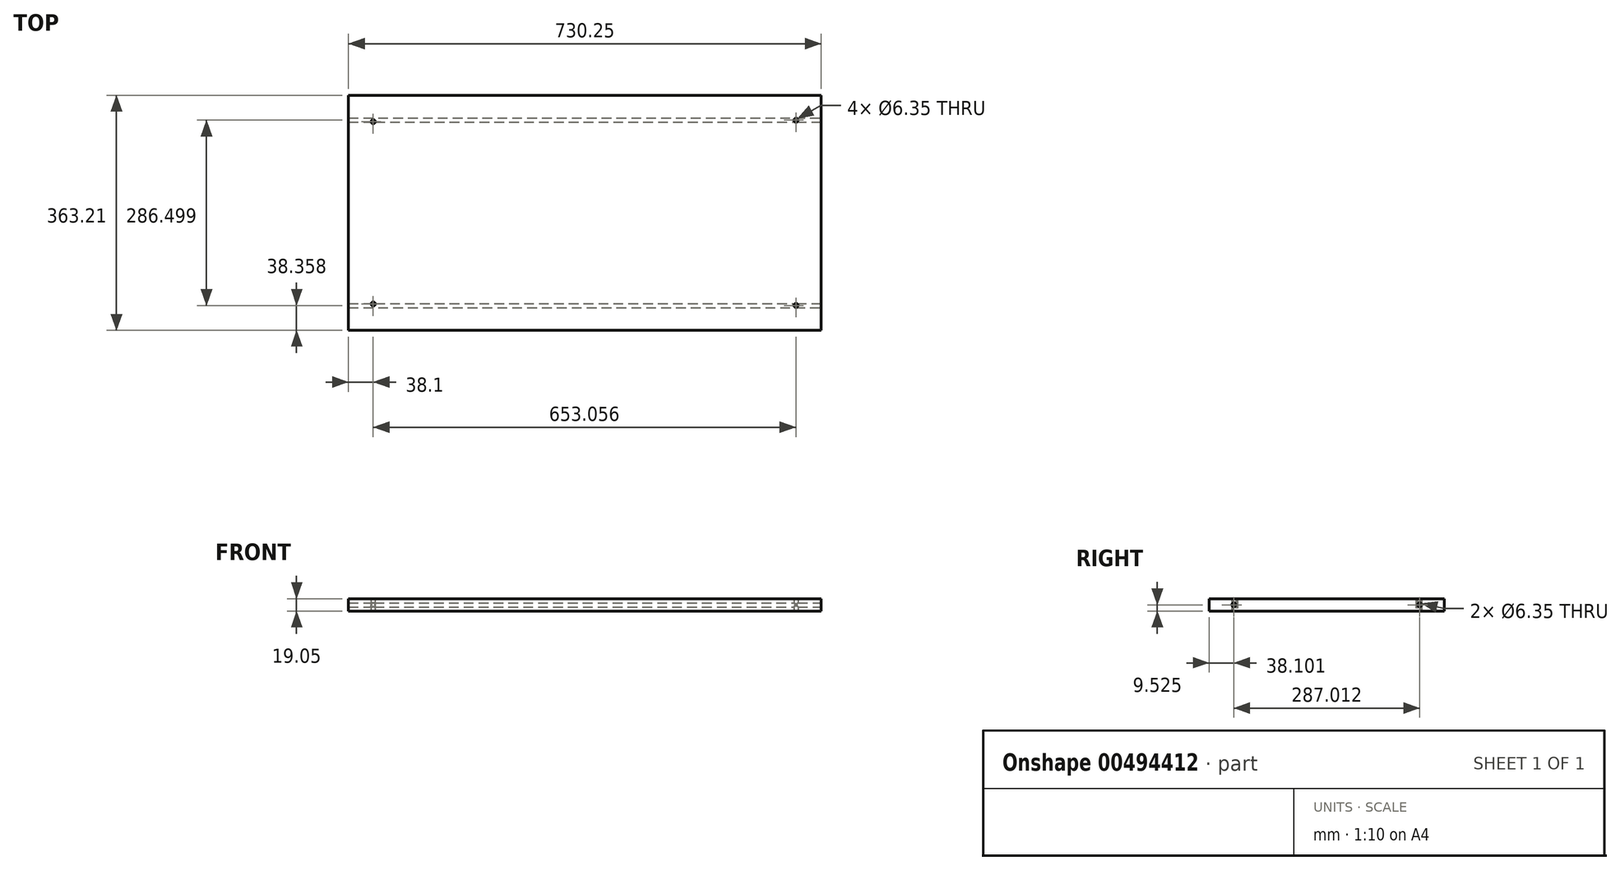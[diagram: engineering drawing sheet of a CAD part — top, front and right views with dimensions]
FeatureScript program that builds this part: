
annotation { "Feature Type Name" : "Feature", "Feature Type Description" : "" }
export const myFeature = defineFeature(function(context is Context, id is Id, definition is map)
    precondition{}
    {
        {
            var Q0;
            Q0=qCreatedBy(makeId("Top.planeOp"),FACE);
            var sketch = newSketch(context, id + "F0", { "sketchPlane" : qUnion([Q0])});
            skLineSegment(sketch, "E0.bottom", {"start": v(-364.5, 180.63) * mm, "end": v(365.76, 180.63) * mm});
            skLineSegment(sketch, "E0.top", {"start": v(-364.5, -182.58) * mm, "end": v(365.76, -182.58) * mm});
            skLineSegment(sketch, "E0.left", {"start": v(-364.5, 180.63) * mm, "end": v(-364.5, -182.58) * mm});
            skLineSegment(sketch, "E0.right", {"start": v(365.76, 180.63) * mm, "end": v(365.76, -182.58) * mm});
            skLineSegment(sketch, "E1", {"start": v(365.76, -0.97) * mm, "end": v(-364.5, -0.97) * mm, "construction": true});
            skLineSegment(sketch, "E2", {"start": v(0.63, -0.97) * mm, "end": v(0, 180.63) * mm, "construction": true});
            skPoint(sketch, "E2.endSnap0", {"position": v(0.63, 180.63) * mm});
            skCircle(sketch, "E3", {"center": v(-326.4, 140) * mm, "radius": 3.18 * mm});
            skCircle(sketch, "E4.MirrorC", {"center": v(326.67, 142.28) * mm, "radius": 3.18 * mm});
            skCircle(sketch, "E5.MirrorC", {"center": v(-326.4, -141.94) * mm, "radius": 3.18 * mm});
            skLineSegment(sketch, "E6.MirrorCS", {"start": v(0.63, -0.97) * mm, "end": v(0, -182.58) * mm, "construction": true});
            skCircle(sketch, "E7.MirrorC", {"center": v(326.67, -144.22) * mm, "radius": 3.18 * mm});
            skSolve(sketch);
        }
        {
            var Q0;
            Q0 = qSketchRegion(id + "F0", true);
            extrude(context, id + "F1", {"entities" : qUnion([Q0]), "depth" : 19.05 * mm, "offsetDistance" : 25.4 * mm});
        }
        {
            var Q0;
            Q0=qCreatedBy(makeId("Right.planeOp"),FACE);
            cPlane(context, id + "F2", {"entities" : qUnion([Q0]), "cplaneType" : CPlaneType.OFFSET, "offset" : 373.38 * mm, "width" : 152.4 * mm, "height" : 152.4 * mm});
        }
        {
            var Q0;
            Q0=qCreatedBy(id+"F2.planeOp",FACE);
            var sketch = newSketch(context, id + "F3", { "sketchPlane" : qUnion([Q0])});
            skPoint(sketch, "E8.0", {"position": v(-0.97, 0) * mm});
            skPoint(sketch, "E9.0", {"position": v(-0.97, 19.05) * mm});
            skLineSegment(sketch, "E10", {"start": v(-0.97, 19.05) * mm, "end": v(-0.97, 0) * mm, "construction": true});
            skPoint(sketch, "E11.0", {"position": v(-182.58, 9.53) * mm});
            skPoint(sketch, "E12.0", {"position": v(180.63, 9.53) * mm});
            skLineSegment(sketch, "E13", {"start": v(180.63, 9.53) * mm, "end": v(-182.58, 9.53) * mm, "construction": true});
            skCircle(sketch, "E14", {"center": v(-144.48, 9.52) * mm, "radius": 3.18 * mm});
            skCircle(sketch, "E15.MirrorC", {"center": v(142.53, 9.52) * mm, "radius": 3.18 * mm});
            skSolve(sketch);
        }
        {
            var Q0;
            Q0 = qSketchRegion(id + "F3", true);
            extrude(context, id + "F4", {"entities" : qUnion([Q0]), "operationType" : NewBodyOperationType.REMOVE, "oppositeDirection" : true, "depth" : 805.43 * mm, "offsetDistance" : 25.4 * mm});
        }
    });
